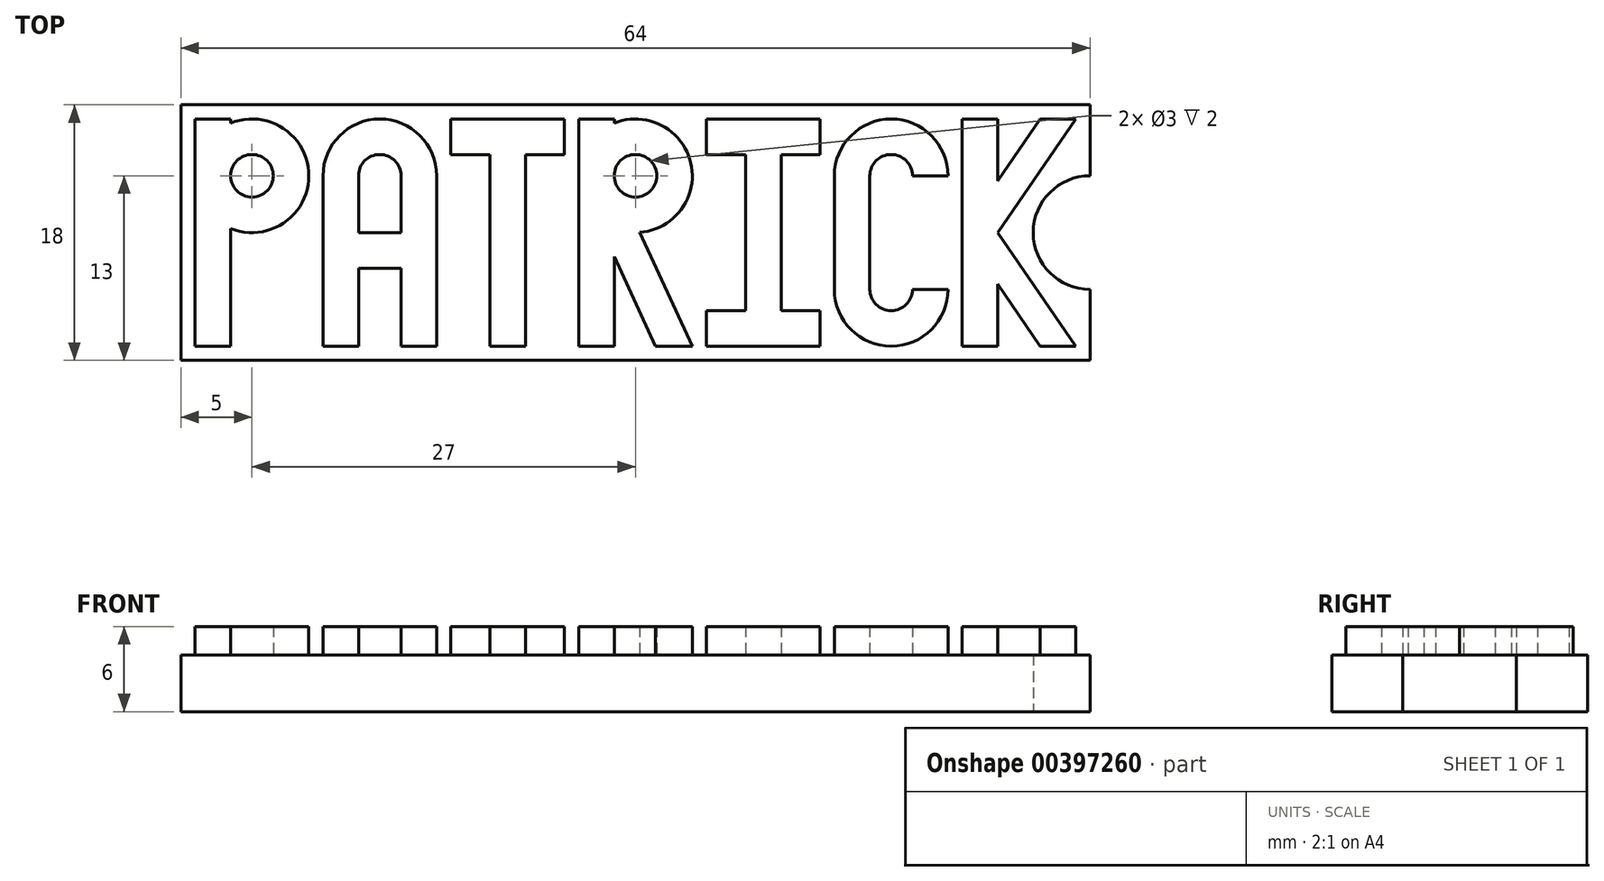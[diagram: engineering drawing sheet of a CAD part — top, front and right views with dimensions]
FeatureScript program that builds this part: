
annotation { "Feature Type Name" : "Feature", "Feature Type Description" : "" }
export const myFeature = defineFeature(function(context is Context, id is Id, definition is map)
    precondition{}
    {
        {
            var Q0;
            Q0=qCreatedBy(makeId("Top.planeOp"),FACE);
            var sketch = newSketch(context, id + "F0", { "sketchPlane" : qUnion([Q0])});
            skLineSegment(sketch, "E0.bottom", {"start": v(0, 0) * mm, "end": v(-64, 0) * mm});
            skLineSegment(sketch, "E0.top", {"start": v(0, 18) * mm, "end": v(-64, 18) * mm});
            skLineSegment(sketch, "E0.left", {"start": v(0, 0) * mm, "end": v(0, 18) * mm});
            skLineSegment(sketch, "E0.right", {"start": v(-64, 0) * mm, "end": v(-64, 18) * mm});
            skCircle(sketch, "E1", {"center": v(0, 9) * mm, "radius": 2 * mm});
            skCircle(sketch, "E2", {"center": v(0, 9) * mm, "radius": 4 * mm});
            skSolve(sketch);
        }
        {
            var Q0;
            Q0=makeQuery(id+"F0.imprint","IMPRINT",FACE,{"disambiguationData":[TD([[makeQuery(id+"F0.imprint","IMPRINT",EDGE,{"derivedFrom":sQuery(id+"F0.wireOp",EDGE,"E0.bottom")}),-1.0]])]});
            var Q1;
            {var subQ0=sQuery(id+"F0.wireOp",EDGE,"E2");var subQ1=sQuery(id+"F0.wireOp",EDGE,"E0.left");var subQ2=makeQuery(id+"F0.imprint","INTERSECT",VERTEX,{"disambiguationData":[OD(0.0)],"derivedFrom":[subQ1,subQ0]});Q1=makeQuery(id+"F0.imprint","IMPRINT",FACE,{"disambiguationData":[TD([[makeQuery(id+"F0.imprint","IMPRINT",EDGE,{"disambiguationData":[TD([[subQ2,-1.0]])],"derivedFrom":subQ1}),1.0]])]});}
            var Q2;
            {var subQ0=sQuery(id+"F0.wireOp",EDGE,"E2");var subQ1=sQuery(id+"F0.wireOp",EDGE,"E0.left");var subQ2=makeQuery(id+"F0.imprint","INTERSECT",VERTEX,{"disambiguationData":[OD(0.0)],"derivedFrom":[subQ1,subQ0]});Q2=makeQuery(id+"F0.imprint","IMPRINT",FACE,{"disambiguationData":[TD([[makeQuery(id+"F0.imprint","IMPRINT",EDGE,{"disambiguationData":[TD([[subQ2,-1.0]])],"derivedFrom":subQ1}),-1.0]])]});}
            extrude(context, id + "F1", {"entities" : qUnion([Q0, Q1, Q2]), "depth" : 4 * mm});
        }
        {
            var Q0;
            Q0=makeQuery(id+"F1.opExtrude","CAP_FACE",FACE,{"disambiguationData":[OSD([sQuery(id+"F0.wireOp",EDGE,"E0.bottom"),sQuery(id+"F0.wireOp",EDGE,"E0.top"),sQuery(id+"F0.wireOp",EDGE,"E0.left"),sQuery(id+"F0.wireOp",EDGE,"E0.right")])],"isStart":false});
            var sketch = newSketch(context, id + "F2", { "sketchPlane" : qUnion([Q0])});
            skLineSegment(sketch, "E3.bottom", {"start": v(-63, 17) * mm, "end": v(-55, 17) * mm, "construction": true});
            skLineSegment(sketch, "E3.top", {"start": v(-63, 1) * mm, "end": v(-55, 1) * mm, "construction": true});
            skLineSegment(sketch, "E3.left", {"start": v(-63, 17) * mm, "end": v(-63, 1) * mm, "construction": true});
            skLineSegment(sketch, "E3.right", {"start": v(-55, 17) * mm, "end": v(-55, 1) * mm, "construction": true});
            skLineSegment(sketch, "E4.bottom", {"start": v(-54, 17) * mm, "end": v(-46, 17) * mm, "construction": true});
            skLineSegment(sketch, "E4.top", {"start": v(-54, 1) * mm, "end": v(-46, 1) * mm, "construction": true});
            skLineSegment(sketch, "E4.left", {"start": v(-54, 17) * mm, "end": v(-54, 1) * mm, "construction": true});
            skLineSegment(sketch, "E4.right", {"start": v(-46, 17) * mm, "end": v(-46, 1) * mm, "construction": true});
            skLineSegment(sketch, "E5.bottom", {"start": v(-45, 17) * mm, "end": v(-37, 17) * mm, "construction": true});
            skLineSegment(sketch, "E5.top", {"start": v(-45, 1) * mm, "end": v(-37, 1) * mm, "construction": true});
            skLineSegment(sketch, "E5.left", {"start": v(-45, 17) * mm, "end": v(-45, 1) * mm, "construction": true});
            skLineSegment(sketch, "E5.right", {"start": v(-37, 17) * mm, "end": v(-37, 1) * mm, "construction": true});
            skLineSegment(sketch, "E6.bottom", {"start": v(-36, 17) * mm, "end": v(-28, 17) * mm, "construction": true});
            skLineSegment(sketch, "E6.top", {"start": v(-36, 1) * mm, "end": v(-28, 1) * mm, "construction": true});
            skLineSegment(sketch, "E6.left", {"start": v(-36, 17) * mm, "end": v(-36, 1) * mm, "construction": true});
            skLineSegment(sketch, "E6.right", {"start": v(-28, 17) * mm, "end": v(-28, 1) * mm, "construction": true});
            skLineSegment(sketch, "E7.bottom", {"start": v(-27, 17) * mm, "end": v(-19, 17) * mm, "construction": true});
            skLineSegment(sketch, "E7.top", {"start": v(-27, 1) * mm, "end": v(-19, 1) * mm, "construction": true});
            skLineSegment(sketch, "E7.left", {"start": v(-27, 17) * mm, "end": v(-27, 1) * mm, "construction": true});
            skLineSegment(sketch, "E7.right", {"start": v(-19, 17) * mm, "end": v(-19, 1) * mm, "construction": true});
            skLineSegment(sketch, "E8.bottom", {"start": v(-18, 17) * mm, "end": v(-10, 17) * mm, "construction": true});
            skLineSegment(sketch, "E8.top", {"start": v(-18, 1) * mm, "end": v(-10, 1) * mm, "construction": true});
            skLineSegment(sketch, "E8.left", {"start": v(-18, 17) * mm, "end": v(-18, 1) * mm, "construction": true});
            skLineSegment(sketch, "E8.right", {"start": v(-10, 17) * mm, "end": v(-10, 1) * mm, "construction": true});
            skLineSegment(sketch, "E9.bottom", {"start": v(-9, 17) * mm, "end": v(-1, 17) * mm, "construction": true});
            skLineSegment(sketch, "E9.top", {"start": v(-9, 1) * mm, "end": v(-1, 1) * mm, "construction": true});
            skLineSegment(sketch, "E9.left", {"start": v(-9, 17) * mm, "end": v(-9, 1) * mm, "construction": true});
            skLineSegment(sketch, "E9.right", {"start": v(-1, 17) * mm, "end": v(-1, 1) * mm, "construction": true});
            skLineSegment(sketch, "E10", {"start": v(-63, 9) * mm, "end": v(-55, 9) * mm, "construction": true});
            skLineSegment(sketch, "E11", {"start": v(-63, 17) * mm, "end": v(-63, 1) * mm});
            skLineSegment(sketch, "E12", {"start": v(-60.5, 17) * mm, "end": v(-60.5, 1) * mm});
            skLineSegment(sketch, "E13", {"start": v(-63, 1) * mm, "end": v(-60.5, 1) * mm});
            skLineSegment(sketch, "E14", {"start": v(-63, 17) * mm, "end": v(-60.5, 17) * mm});
            skLineSegment(sketch, "E15", {"start": v(-63, 9) * mm, "end": v(-55, 17) * mm, "construction": true});
            skLineSegment(sketch, "E16", {"start": v(-63, 17) * mm, "end": v(-55, 9) * mm, "construction": true});
            skCircle(sketch, "E17", {"center": v(-59, 13) * mm, "radius": 4 * mm});
            skCircle(sketch, "E18", {"center": v(-59, 13) * mm, "radius": 1.5 * mm});
            skLineSegment(sketch, "E19", {"start": v(-54, 17) * mm, "end": v(-54, 1) * mm});
            skLineSegment(sketch, "E20", {"start": v(-46, 17) * mm, "end": v(-46, 1) * mm});
            skLineSegment(sketch, "E21", {"start": v(-51.5, 17) * mm, "end": v(-51.5, 1) * mm});
            skLineSegment(sketch, "E22", {"start": v(-54, 1) * mm, "end": v(-51.5, 1) * mm});
            skLineSegment(sketch, "E23", {"start": v(-48.5, 17) * mm, "end": v(-48.5, 1) * mm});
            skLineSegment(sketch, "E24", {"start": v(-48.5, 1) * mm, "end": v(-46, 1) * mm});
            skLineSegment(sketch, "E25", {"start": v(-54, 9) * mm, "end": v(-46, 9) * mm});
            skLineSegment(sketch, "E26", {"start": v(-54, 6.5) * mm, "end": v(-46, 6.5) * mm});
            skLineSegment(sketch, "E27", {"start": v(-54, 9) * mm, "end": v(-46, 17) * mm, "construction": true});
            skLineSegment(sketch, "E28", {"start": v(-54, 17) * mm, "end": v(-46, 9) * mm, "construction": true});
            skCircle(sketch, "E29", {"center": v(-50, 13) * mm, "radius": 4 * mm});
            skCircle(sketch, "E30", {"center": v(-50, 13) * mm, "radius": 1.5 * mm});
            skLineSegment(sketch, "E31", {"start": v(-45, 17) * mm, "end": v(-37, 17) * mm});
            skLineSegment(sketch, "E32", {"start": v(-45, 14.5) * mm, "end": v(-37, 14.5) * mm});
            skLineSegment(sketch, "E33", {"start": v(-45, 17) * mm, "end": v(-45, 14.5) * mm});
            skLineSegment(sketch, "E34", {"start": v(-37, 17) * mm, "end": v(-37, 14.5) * mm});
            skLineSegment(sketch, "E35", {"start": v(-42.25, 17) * mm, "end": v(-42.25, 1) * mm});
            skLineSegment(sketch, "E36", {"start": v(-39.75, 17) * mm, "end": v(-39.75, 1) * mm});
            skLineSegment(sketch, "E37", {"start": v(-42.25, 1) * mm, "end": v(-39.75, 1) * mm});
            skLineSegment(sketch, "E38", {"start": v(-36, 17) * mm, "end": v(-36, 1) * mm});
            skLineSegment(sketch, "E39", {"start": v(-33.5, 17) * mm, "end": v(-33.5, 1) * mm});
            skLineSegment(sketch, "E40", {"start": v(-36, 17) * mm, "end": v(-33.5, 17) * mm});
            skLineSegment(sketch, "E41", {"start": v(-36, 1) * mm, "end": v(-33.5, 1) * mm});
            skLineSegment(sketch, "E42", {"start": v(-36, 9) * mm, "end": v(-28, 9) * mm, "construction": true});
            skLineSegment(sketch, "E43", {"start": v(-28, 17) * mm, "end": v(-36, 9) * mm, "construction": true});
            skLineSegment(sketch, "E44", {"start": v(-36, 17) * mm, "end": v(-28, 9) * mm, "construction": true});
            skCircle(sketch, "E45", {"center": v(-32, 13) * mm, "radius": 4 * mm});
            skCircle(sketch, "E46", {"center": v(-32, 13) * mm, "radius": 1.5 * mm});
            skLineSegment(sketch, "E47", {"start": v(-33.06, 11.94) * mm, "end": v(-28, 1) * mm});
            skLineSegment(sketch, "E48", {"start": v(-34.83, 10.17) * mm, "end": v(-30.59, 1) * mm});
            skLineSegment(sketch, "E49", {"start": v(-30.59, 1) * mm, "end": v(-28, 1) * mm});
            skLineSegment(sketch, "E50", {"start": v(-27, 17) * mm, "end": v(-19, 17) * mm});
            skLineSegment(sketch, "E51", {"start": v(-27, 14.5) * mm, "end": v(-19, 14.5) * mm});
            skLineSegment(sketch, "E52", {"start": v(-27, 17) * mm, "end": v(-27, 14.5) * mm});
            skLineSegment(sketch, "E53", {"start": v(-19, 17) * mm, "end": v(-19, 14.5) * mm});
            skLineSegment(sketch, "E54", {"start": v(-27, 1) * mm, "end": v(-19, 1) * mm});
            skLineSegment(sketch, "E55", {"start": v(-27, 3.5) * mm, "end": v(-19, 3.5) * mm});
            skLineSegment(sketch, "E56", {"start": v(-27, 3.5) * mm, "end": v(-27, 1) * mm});
            skLineSegment(sketch, "E57", {"start": v(-19, 3.5) * mm, "end": v(-19, 1) * mm});
            skLineSegment(sketch, "E58", {"start": v(-24.25, 17) * mm, "end": v(-24.25, 1) * mm});
            skLineSegment(sketch, "E59", {"start": v(-21.75, 17) * mm, "end": v(-21.75, 1) * mm});
            skLineSegment(sketch, "E60", {"start": v(-18, 17) * mm, "end": v(-18, 1) * mm});
            skLineSegment(sketch, "E61", {"start": v(-15.5, 17) * mm, "end": v(-15.5, 1) * mm});
            skLineSegment(sketch, "E62", {"start": v(-18, 9) * mm, "end": v(-10, 9) * mm, "construction": true});
            skLineSegment(sketch, "E63", {"start": v(-18, 9) * mm, "end": v(-10, 17) * mm, "construction": true});
            skLineSegment(sketch, "E64", {"start": v(-18, 17) * mm, "end": v(-10, 9) * mm, "construction": true});
            skLineSegment(sketch, "E65", {"start": v(-18, 1) * mm, "end": v(-10, 9) * mm, "construction": true});
            skLineSegment(sketch, "E66", {"start": v(-18, 9) * mm, "end": v(-10, 1) * mm, "construction": true});
            skCircle(sketch, "E67", {"center": v(-14, 13) * mm, "radius": 4 * mm});
            skCircle(sketch, "E68", {"center": v(-14, 13) * mm, "radius": 1.5 * mm});
            skCircle(sketch, "E69", {"center": v(-14, 5) * mm, "radius": 4 * mm});
            skCircle(sketch, "E70", {"center": v(-14, 5) * mm, "radius": 1.5 * mm});
            skLineSegment(sketch, "E71", {"start": v(-10, 5) * mm, "end": v(-12.5, 5) * mm});
            skLineSegment(sketch, "E72", {"start": v(-10, 13) * mm, "end": v(-12.5, 13) * mm});
            skLineSegment(sketch, "E73", {"start": v(-9, 17) * mm, "end": v(-9, 1) * mm});
            skLineSegment(sketch, "E74", {"start": v(-6.5, 17) * mm, "end": v(-6.5, 1) * mm});
            skLineSegment(sketch, "E75", {"start": v(-9, 1) * mm, "end": v(-6.5, 1) * mm});
            skLineSegment(sketch, "E76", {"start": v(-9, 17) * mm, "end": v(-6.5, 17) * mm});
            skLineSegment(sketch, "E77", {"start": v(-9, 9) * mm, "end": v(-1, 9) * mm, "construction": true});
            skLineSegment(sketch, "E78", {"start": v(-9, 6.5) * mm, "end": v(-1, 6.5) * mm, "construction": true});
            skLineSegment(sketch, "E79", {"start": v(-6.5, 9) * mm, "end": v(-1, 17) * mm});
            skLineSegment(sketch, "E80", {"start": v(-9, 9) * mm, "end": v(-3.5, 17) * mm});
            skLineSegment(sketch, "E81", {"start": v(-3.5, 17) * mm, "end": v(-1, 17) * mm});
            skLineSegment(sketch, "E82", {"start": v(-6.5, 9) * mm, "end": v(-1, 1) * mm});
            skLineSegment(sketch, "E83", {"start": v(-9, 9) * mm, "end": v(-3.5, 1) * mm});
            skLineSegment(sketch, "E84", {"start": v(-3.5, 1) * mm, "end": v(-1, 1) * mm});
            skSolve(sketch);
        }
        {
            var Q0;
            {var subQ0=sQuery(id+"F2.wireOp",EDGE,"E12");var subQ1=makeQuery(id+"F2.imprint","INTERSECT",VERTEX,{"derivedFrom":[subQ0,sQuery(id+"F2.wireOp",EDGE,"E18")]});Q0=makeQuery(id+"F2.imprint","IMPRINT",FACE,{"disambiguationData":[TD([[makeQuery(id+"F2.imprint","IMPRINT",EDGE,{"disambiguationData":[TD([[subQ1,1.0]])],"derivedFrom":subQ0}),-1.0]])]});}
            var Q1;
            {var subQ0=sQuery(id+"F2.wireOp",EDGE,"E14");Q1=makeQuery(id+"F2.imprint","IMPRINT",FACE,{"disambiguationData":[TD([[makeQuery(id+"F2.imprint","IMPRINT",EDGE,{"derivedFrom":subQ0}),-1.0]])]});}
            var Q2;
            {var subQ0=sQuery(id+"F2.wireOp",EDGE,"E13");Q2=makeQuery(id+"F2.imprint","IMPRINT",FACE,{"disambiguationData":[TD([[makeQuery(id+"F2.imprint","IMPRINT",EDGE,{"derivedFrom":subQ0}),1.0]])]});}
            var Q3;
            {var subQ0=sQuery(id+"F2.wireOp",EDGE,"E18");Q3=makeQuery(id+"F2.imprint","IMPRINT",FACE,{"disambiguationData":[TD([[makeQuery(id+"F2.imprint","IMPRINT",EDGE,{"derivedFrom":subQ0}),-1.0]])]});}
            var Q4;
            {var subQ0=sQuery(id+"F2.wireOp",EDGE,"E29");var subQ1=sQuery(id+"F2.wireOp",EDGE,"E21");var subQ2=makeQuery(id+"F2.imprint","INTERSECT",VERTEX,{"disambiguationData":[OD(0.0)],"derivedFrom":[subQ1,subQ0]});Q4=makeQuery(id+"F2.imprint","IMPRINT",FACE,{"disambiguationData":[TD([[makeQuery(id+"F2.imprint","IMPRINT",EDGE,{"disambiguationData":[TD([[subQ2,-1.0]])],"derivedFrom":subQ1}),-1.0]])]});}
            var Q5;
            {var subQ0=sQuery(id+"F2.wireOp",EDGE,"E29");var subQ1=sQuery(id+"F2.wireOp",EDGE,"E21");var subQ2=makeQuery(id+"F2.imprint","INTERSECT",VERTEX,{"disambiguationData":[OD(0.0)],"derivedFrom":[subQ1,subQ0]});Q5=makeQuery(id+"F2.imprint","IMPRINT",FACE,{"disambiguationData":[TD([[makeQuery(id+"F2.imprint","IMPRINT",EDGE,{"disambiguationData":[TD([[subQ2,-1.0]])],"derivedFrom":subQ1}),1.0]])]});}
            var Q6;
            {var subQ0=sQuery(id+"F2.wireOp",EDGE,"E29");var subQ1=sQuery(id+"F2.wireOp",EDGE,"E23");var subQ2=makeQuery(id+"F2.imprint","INTERSECT",VERTEX,{"disambiguationData":[OD(0.0)],"derivedFrom":[subQ1,subQ0]});Q6=makeQuery(id+"F2.imprint","IMPRINT",FACE,{"disambiguationData":[TD([[makeQuery(id+"F2.imprint","IMPRINT",EDGE,{"disambiguationData":[TD([[subQ2,-1.0]])],"derivedFrom":subQ1}),1.0]])]});}
            var Q7;
            {var subQ0=sQuery(id+"F2.wireOp",EDGE,"E25");var subQ4=sQuery(id+"F2.wireOp",EDGE,"E21");var subQ5=makeQuery(id+"F2.imprint","INTERSECT",VERTEX,{"derivedFrom":[subQ4,subQ0]});Q7=makeQuery(id+"F2.imprint","IMPRINT",FACE,{"disambiguationData":[TD([[makeQuery(id+"F2.imprint","IMPRINT",EDGE,{"disambiguationData":[TD([[subQ5,-1.0]])],"derivedFrom":subQ4}),1.0]])]});}
            var Q8;
            {var subQ0=sQuery(id+"F2.wireOp",EDGE,"E25");var subQ1=sQuery(id+"F2.wireOp",EDGE,"E19");var subQ2=makeQuery(id+"F2.imprint","INTERSECT",VERTEX,{"derivedFrom":[subQ1,subQ0]});Q8=makeQuery(id+"F2.imprint","IMPRINT",FACE,{"disambiguationData":[TD([[makeQuery(id+"F2.imprint","IMPRINT",EDGE,{"disambiguationData":[TD([[subQ2,-1.0]])],"derivedFrom":subQ1}),1.0]])]});}
            var Q9;
            {var subQ0=sQuery(id+"F2.wireOp",EDGE,"E25");var subQ1=sQuery(id+"F2.wireOp",EDGE,"E19");var subQ2=makeQuery(id+"F2.imprint","INTERSECT",VERTEX,{"derivedFrom":[subQ1,subQ0]});Q9=makeQuery(id+"F2.imprint","IMPRINT",FACE,{"disambiguationData":[TD([[makeQuery(id+"F2.imprint","IMPRINT",EDGE,{"disambiguationData":[TD([[subQ2,1.0]])],"derivedFrom":subQ1}),1.0]])]});}
            var Q10;
            {var subQ0=sQuery(id+"F2.wireOp",EDGE,"E25");var subQ1=sQuery(id+"F2.wireOp",EDGE,"E20");var subQ2=makeQuery(id+"F2.imprint","INTERSECT",VERTEX,{"derivedFrom":[subQ1,subQ0]});Q10=makeQuery(id+"F2.imprint","IMPRINT",FACE,{"disambiguationData":[TD([[makeQuery(id+"F2.imprint","IMPRINT",EDGE,{"disambiguationData":[TD([[subQ2,1.0]])],"derivedFrom":subQ1}),-1.0]])]});}
            var Q11;
            {var subQ0=sQuery(id+"F2.wireOp",EDGE,"E25");var subQ1=sQuery(id+"F2.wireOp",EDGE,"E20");var subQ2=makeQuery(id+"F2.imprint","INTERSECT",VERTEX,{"derivedFrom":[subQ1,subQ0]});Q11=makeQuery(id+"F2.imprint","IMPRINT",FACE,{"disambiguationData":[TD([[makeQuery(id+"F2.imprint","IMPRINT",EDGE,{"disambiguationData":[TD([[subQ2,-1.0]])],"derivedFrom":subQ1}),-1.0]])]});}
            var Q12;
            {var subQ0=sQuery(id+"F2.wireOp",EDGE,"E24");Q12=makeQuery(id+"F2.imprint","IMPRINT",FACE,{"disambiguationData":[TD([[makeQuery(id+"F2.imprint","IMPRINT",EDGE,{"derivedFrom":subQ0}),1.0]])]});}
            var Q13;
            {var subQ0=sQuery(id+"F2.wireOp",EDGE,"E22");Q13=makeQuery(id+"F2.imprint","IMPRINT",FACE,{"disambiguationData":[TD([[makeQuery(id+"F2.imprint","IMPRINT",EDGE,{"derivedFrom":subQ0}),1.0]])]});}
            var Q14;
            {var subQ5=sQuery(id+"F2.wireOp",EDGE,"E37");Q14=makeQuery(id+"F2.imprint","IMPRINT",FACE,{"disambiguationData":[TD([[makeQuery(id+"F2.imprint","IMPRINT",EDGE,{"derivedFrom":subQ5}),1.0]])]});}
            var Q15;
            {var subQ0=sQuery(id+"F2.wireOp",EDGE,"E33");Q15=makeQuery(id+"F2.imprint","IMPRINT",FACE,{"disambiguationData":[TD([[makeQuery(id+"F2.imprint","IMPRINT",EDGE,{"derivedFrom":subQ0}),1.0]])]});}
            var Q16;
            {var subQ0=sQuery(id+"F2.wireOp",EDGE,"E35");var subQ1=sQuery(id+"F2.wireOp",EDGE,"E31");var subQ2=makeQuery(id+"F2.imprint","INTERSECT",VERTEX,{"derivedFrom":[subQ1,subQ0]});Q16=makeQuery(id+"F2.imprint","IMPRINT",FACE,{"disambiguationData":[TD([[makeQuery(id+"F2.imprint","IMPRINT",EDGE,{"disambiguationData":[TD([[subQ2,-1.0]])],"derivedFrom":subQ1}),-1.0]])]});}
            var Q17;
            {var subQ0=sQuery(id+"F2.wireOp",EDGE,"E34");Q17=makeQuery(id+"F2.imprint","IMPRINT",FACE,{"disambiguationData":[TD([[makeQuery(id+"F2.imprint","IMPRINT",EDGE,{"derivedFrom":subQ0}),-1.0]])]});}
            var Q18;
            {var subQ0=sQuery(id+"F2.wireOp",EDGE,"E45");var subQ3=sQuery(id+"F2.wireOp",EDGE,"E39");var subQ4=makeQuery(id+"F2.imprint","INTERSECT",VERTEX,{"disambiguationData":[OD(0.0)],"derivedFrom":[subQ3,subQ0]});Q18=makeQuery(id+"F2.imprint","IMPRINT",FACE,{"disambiguationData":[TD([[makeQuery(id+"F2.imprint","IMPRINT",EDGE,{"disambiguationData":[TD([[subQ4,-1.0]])],"derivedFrom":subQ3}),-1.0]])]});}
            var Q19;
            {var subQ0=sQuery(id+"F2.wireOp",EDGE,"E40");Q19=makeQuery(id+"F2.imprint","IMPRINT",FACE,{"disambiguationData":[TD([[makeQuery(id+"F2.imprint","IMPRINT",EDGE,{"derivedFrom":subQ0}),-1.0]])]});}
            var Q20;
            {var subQ5=sQuery(id+"F2.wireOp",EDGE,"E41");Q20=makeQuery(id+"F2.imprint","IMPRINT",FACE,{"disambiguationData":[TD([[makeQuery(id+"F2.imprint","IMPRINT",EDGE,{"derivedFrom":subQ5}),1.0]])]});}
            var Q21;
            {var subQ0=sQuery(id+"F2.wireOp",EDGE,"E45");var subQ1=sQuery(id+"F2.wireOp",EDGE,"E39");var subQ2=makeQuery(id+"F2.imprint","INTERSECT",VERTEX,{"disambiguationData":[OD(1.0)],"derivedFrom":[subQ1,subQ0]});Q21=makeQuery(id+"F2.imprint","IMPRINT",FACE,{"disambiguationData":[TD([[makeQuery(id+"F2.imprint","IMPRINT",EDGE,{"disambiguationData":[TD([[subQ2,-1.0]])],"derivedFrom":subQ1}),-1.0]])]});}
            var Q22;
            {var subQ0=sQuery(id+"F2.wireOp",EDGE,"E49");Q22=makeQuery(id+"F2.imprint","IMPRINT",FACE,{"disambiguationData":[TD([[makeQuery(id+"F2.imprint","IMPRINT",EDGE,{"derivedFrom":subQ0}),1.0]])]});}
            var Q23;
            {var subQ0=sQuery(id+"F2.wireOp",EDGE,"E46");var subQ1=sQuery(id+"F2.wireOp",EDGE,"E39");var subQ2=makeQuery(id+"F2.imprint","INTERSECT",VERTEX,{"derivedFrom":[subQ1,subQ0]});Q23=makeQuery(id+"F2.imprint","IMPRINT",FACE,{"disambiguationData":[TD([[makeQuery(id+"F2.imprint","IMPRINT",EDGE,{"disambiguationData":[TD([[subQ2,-1.0]])],"derivedFrom":subQ1}),1.0]])]});}
            var Q24;
            {var subQ0=sQuery(id+"F2.wireOp",EDGE,"E45");var subQ1=sQuery(id+"F2.wireOp",EDGE,"E39");var subQ2=makeQuery(id+"F2.imprint","INTERSECT",VERTEX,{"disambiguationData":[OD(0.0)],"derivedFrom":[subQ1,subQ0]});Q24=makeQuery(id+"F2.imprint","IMPRINT",FACE,{"disambiguationData":[TD([[makeQuery(id+"F2.imprint","IMPRINT",EDGE,{"disambiguationData":[TD([[subQ2,-1.0]])],"derivedFrom":subQ1}),1.0]])]});}
            var Q25;
            {var subQ0=sQuery(id+"F2.wireOp",EDGE,"E52");Q25=makeQuery(id+"F2.imprint","IMPRINT",FACE,{"disambiguationData":[TD([[makeQuery(id+"F2.imprint","IMPRINT",EDGE,{"derivedFrom":subQ0}),1.0]])]});}
            var Q26;
            {var subQ0=sQuery(id+"F2.wireOp",EDGE,"E58");var subQ1=sQuery(id+"F2.wireOp",EDGE,"E50");var subQ2=makeQuery(id+"F2.imprint","INTERSECT",VERTEX,{"derivedFrom":[subQ1,subQ0]});Q26=makeQuery(id+"F2.imprint","IMPRINT",FACE,{"disambiguationData":[TD([[makeQuery(id+"F2.imprint","IMPRINT",EDGE,{"disambiguationData":[TD([[subQ2,-1.0]])],"derivedFrom":subQ1}),-1.0]])]});}
            var Q27;
            {var subQ0=sQuery(id+"F2.wireOp",EDGE,"E53");Q27=makeQuery(id+"F2.imprint","IMPRINT",FACE,{"disambiguationData":[TD([[makeQuery(id+"F2.imprint","IMPRINT",EDGE,{"derivedFrom":subQ0}),-1.0]])]});}
            var Q28;
            {var subQ0=sQuery(id+"F2.wireOp",EDGE,"E58");var subQ1=sQuery(id+"F2.wireOp",EDGE,"E51");var subQ2=makeQuery(id+"F2.imprint","INTERSECT",VERTEX,{"derivedFrom":[subQ1,subQ0]});Q28=makeQuery(id+"F2.imprint","IMPRINT",FACE,{"disambiguationData":[TD([[makeQuery(id+"F2.imprint","IMPRINT",EDGE,{"disambiguationData":[TD([[subQ2,-1.0]])],"derivedFrom":subQ1}),-1.0]])]});}
            var Q29;
            {var subQ0=sQuery(id+"F2.wireOp",EDGE,"E56");Q29=makeQuery(id+"F2.imprint","IMPRINT",FACE,{"disambiguationData":[TD([[makeQuery(id+"F2.imprint","IMPRINT",EDGE,{"derivedFrom":subQ0}),1.0]])]});}
            var Q30;
            {var subQ0=sQuery(id+"F2.wireOp",EDGE,"E58");var subQ1=sQuery(id+"F2.wireOp",EDGE,"E54");var subQ2=makeQuery(id+"F2.imprint","INTERSECT",VERTEX,{"derivedFrom":[subQ1,subQ0]});Q30=makeQuery(id+"F2.imprint","IMPRINT",FACE,{"disambiguationData":[TD([[makeQuery(id+"F2.imprint","IMPRINT",EDGE,{"disambiguationData":[TD([[subQ2,-1.0]])],"derivedFrom":subQ1}),1.0]])]});}
            var Q31;
            {var subQ0=sQuery(id+"F2.wireOp",EDGE,"E57");Q31=makeQuery(id+"F2.imprint","IMPRINT",FACE,{"disambiguationData":[TD([[makeQuery(id+"F2.imprint","IMPRINT",EDGE,{"derivedFrom":subQ0}),-1.0]])]});}
            var Q32;
            {var subQ0=sQuery(id+"F2.wireOp",EDGE,"E67");var subQ1=sQuery(id+"F2.wireOp",EDGE,"E61");var subQ2=makeQuery(id+"F2.imprint","INTERSECT",VERTEX,{"disambiguationData":[OD(0.0)],"derivedFrom":[subQ1,subQ0]});Q32=makeQuery(id+"F2.imprint","IMPRINT",FACE,{"disambiguationData":[TD([[makeQuery(id+"F2.imprint","IMPRINT",EDGE,{"disambiguationData":[TD([[subQ2,-1.0]])],"derivedFrom":subQ1}),-1.0]])]});}
            var Q33;
            {var subQ0=sQuery(id+"F2.wireOp",EDGE,"E67");var subQ1=sQuery(id+"F2.wireOp",EDGE,"E60");var subQ2=makeQuery(id+"F2.imprint","INTERSECT",VERTEX,{"derivedFrom":[subQ1,subQ0]});Q33=makeQuery(id+"F2.imprint","IMPRINT",FACE,{"disambiguationData":[TD([[makeQuery(id+"F2.imprint","IMPRINT",EDGE,{"disambiguationData":[TD([[subQ2,-1.0]])],"derivedFrom":subQ1}),1.0]])]});}
            var Q34;
            {var subQ0=sQuery(id+"F2.wireOp",EDGE,"E69");var subQ1=sQuery(id+"F2.wireOp",EDGE,"E61");var subQ2=makeQuery(id+"F2.imprint","INTERSECT",VERTEX,{"disambiguationData":[OD(1.0)],"derivedFrom":[subQ1,subQ0]});Q34=makeQuery(id+"F2.imprint","IMPRINT",FACE,{"disambiguationData":[TD([[makeQuery(id+"F2.imprint","IMPRINT",EDGE,{"disambiguationData":[TD([[subQ2,-1.0]])],"derivedFrom":subQ1}),-1.0]])]});}
            var Q35;
            {var subQ5=sQuery(id+"F2.wireOp",EDGE,"E71");Q35=makeQuery(id+"F2.imprint","IMPRINT",FACE,{"disambiguationData":[TD([[makeQuery(id+"F2.imprint","IMPRINT",EDGE,{"derivedFrom":subQ5}),1.0]])]});}
            var Q36;
            {var subQ5=sQuery(id+"F2.wireOp",EDGE,"E72");Q36=makeQuery(id+"F2.imprint","IMPRINT",FACE,{"disambiguationData":[TD([[makeQuery(id+"F2.imprint","IMPRINT",EDGE,{"derivedFrom":subQ5}),-1.0]])]});}
            var Q37;
            {var subQ0=sQuery(id+"F2.wireOp",EDGE,"E76");Q37=makeQuery(id+"F2.imprint","IMPRINT",FACE,{"disambiguationData":[TD([[makeQuery(id+"F2.imprint","IMPRINT",EDGE,{"derivedFrom":subQ0}),-1.0]])]});}
            var Q38;
            {var subQ0=sQuery(id+"F2.wireOp",EDGE,"E74");var subQ2=sQuery(id+"F2.wireOp",EDGE,"E80");var subQ3=makeQuery(id+"F2.imprint","INTERSECT",VERTEX,{"derivedFrom":[subQ0,subQ2]});Q38=makeQuery(id+"F2.imprint","IMPRINT",FACE,{"disambiguationData":[TD([[makeQuery(id+"F2.imprint","IMPRINT",EDGE,{"disambiguationData":[TD([[subQ3,-1.0]])],"derivedFrom":subQ0}),-1.0]])]});}
            var Q39;
            {var subQ0=sQuery(id+"F2.wireOp",EDGE,"E75");Q39=makeQuery(id+"F2.imprint","IMPRINT",FACE,{"disambiguationData":[TD([[makeQuery(id+"F2.imprint","IMPRINT",EDGE,{"derivedFrom":subQ0}),1.0]])]});}
            var Q40;
            {var subQ0=sQuery(id+"F2.wireOp",EDGE,"E82");Q40=makeQuery(id+"F2.imprint","IMPRINT",FACE,{"disambiguationData":[TD([[makeQuery(id+"F2.imprint","IMPRINT",EDGE,{"derivedFrom":subQ0}),-1.0]])]});}
            var Q41;
            {var subQ0=sQuery(id+"F2.wireOp",EDGE,"E79");Q41=makeQuery(id+"F2.imprint","IMPRINT",FACE,{"disambiguationData":[TD([[makeQuery(id+"F2.imprint","IMPRINT",EDGE,{"derivedFrom":subQ0}),1.0]])]});}
            extrude(context, id + "F3", {"entities" : qUnion([Q0, Q1, Q2, Q3, Q4, Q5, Q6, Q7, Q8, Q9, Q10, Q11, Q12, Q13, Q14, Q15, Q16, Q17, Q18, Q19, Q20, Q21, Q22, Q23, Q24, Q25, Q26, Q27, Q28, Q29, Q30, Q31, Q32, Q33, Q34, Q35, Q36, Q37, Q38, Q39, Q40, Q41]), "operationType" : NewBodyOperationType.ADD, "depth" : 2 * mm});
        }
    });
